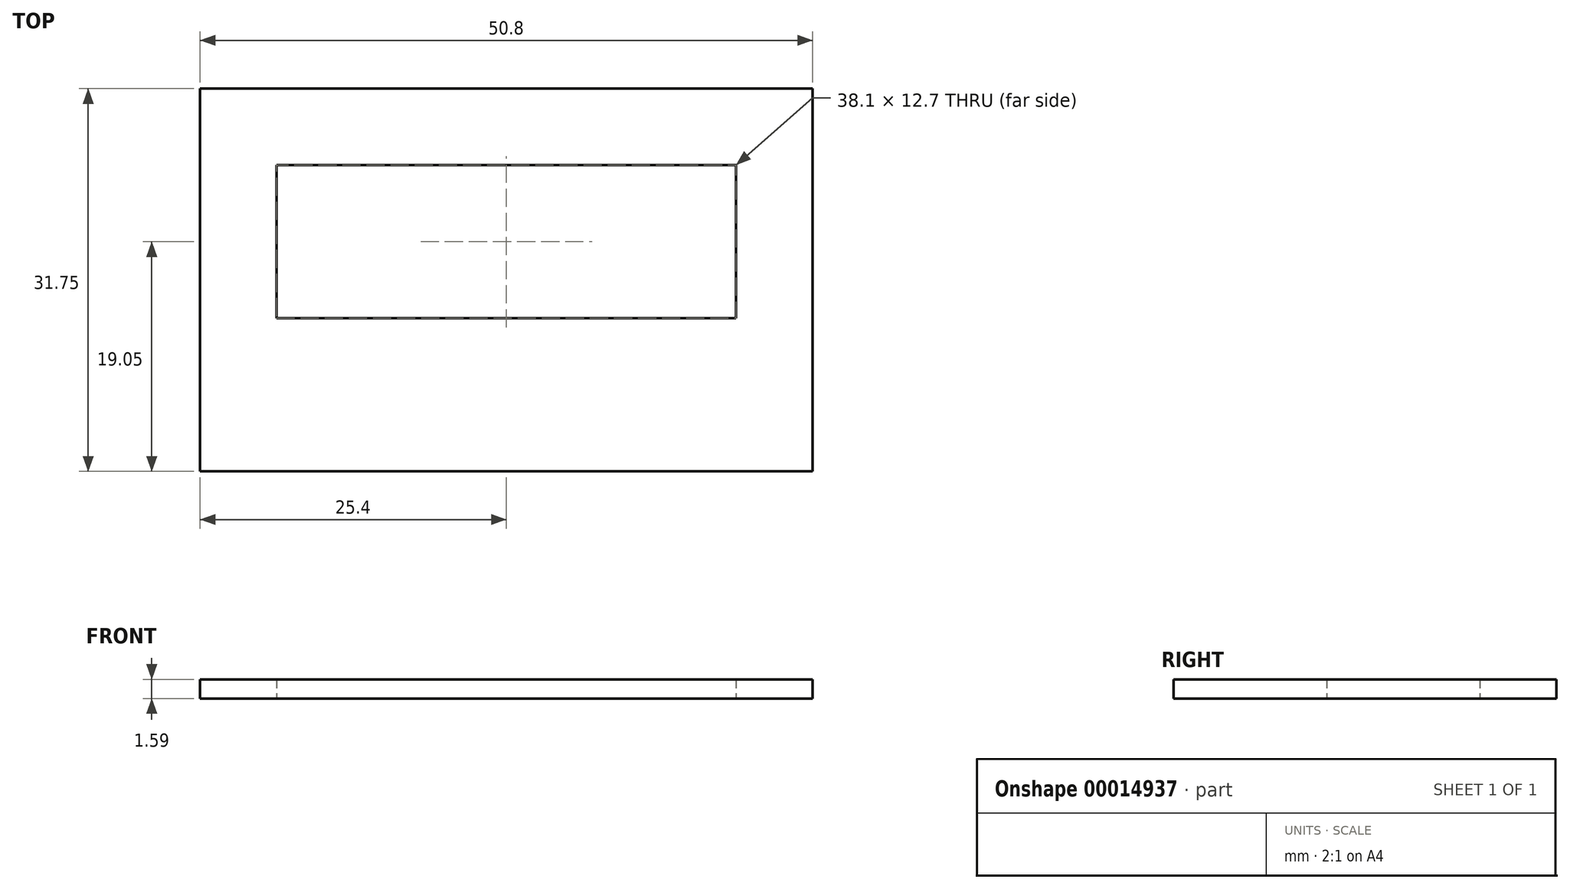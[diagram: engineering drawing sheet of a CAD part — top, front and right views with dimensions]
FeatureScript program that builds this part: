
annotation { "Feature Type Name" : "Feature", "Feature Type Description" : "" }
export const myFeature = defineFeature(function(context is Context, id is Id, definition is map)
    precondition{}
    {
        {
            var Q0;
            Q0=qCreatedBy(makeId("Top.planeOp"),FACE);
            var sketch = newSketch(context, id + "F0", { "sketchPlane" : qUnion([Q0])});
            skLineSegment(sketch, "E0.bottom", {"start": v(0, 31.75) * mm, "end": v(50.8, 31.75) * mm});
            skLineSegment(sketch, "E0.top", {"start": v(0, 0) * mm, "end": v(50.8, 0) * mm});
            skLineSegment(sketch, "E0.left", {"start": v(0, 31.75) * mm, "end": v(0, 0) * mm});
            skLineSegment(sketch, "E0.right", {"start": v(50.8, 31.75) * mm, "end": v(50.8, 0) * mm});
            skLineSegment(sketch, "E1.bottom", {"start": v(6.35, 12.7) * mm, "end": v(44.45, 12.7) * mm});
            skLineSegment(sketch, "E1.top", {"start": v(6.35, 25.4) * mm, "end": v(44.45, 25.4) * mm});
            skLineSegment(sketch, "E1.left", {"start": v(6.35, 12.7) * mm, "end": v(6.35, 25.4) * mm});
            skLineSegment(sketch, "E1.right", {"start": v(44.45, 12.7) * mm, "end": v(44.45, 25.4) * mm});
            skSolve(sketch);
        }
        {
            var Q0;
            Q0=makeQuery(id+"F0.imprint","IMPRINT",FACE,{"disambiguationData":[TD([[makeQuery(id+"F0.imprint","IMPRINT",EDGE,{"derivedFrom":sQuery(id+"F0.wireOp",EDGE,"E0.bottom")}),-1.0]])]});
            extrude(context, id + "F1", {"entities" : qUnion([Q0]), "depth" : 1.59 * mm});
        }
    });
